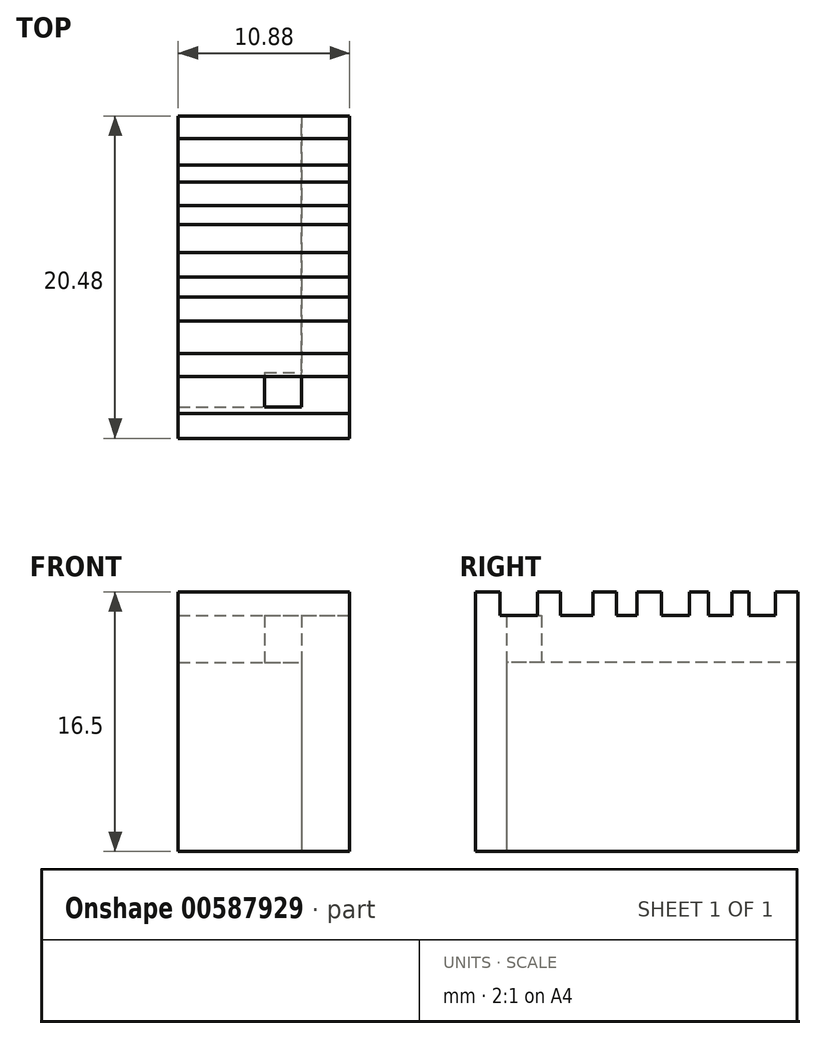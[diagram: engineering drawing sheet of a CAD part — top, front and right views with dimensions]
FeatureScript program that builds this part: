
annotation { "Feature Type Name" : "Feature", "Feature Type Description" : "" }
export const myFeature = defineFeature(function(context is Context, id is Id, definition is map)
    precondition{}
    {
        {
            var Q0;
            Q0=qCreatedBy(makeId("Top.planeOp"),FACE);
            var sketch = newSketch(context, id + "F0", { "sketchPlane" : qUnion([Q0])});
            skLineSegment(sketch, "E0.bottom", {"start": v(-21.97, 0.96) * mm, "end": v(-16.47, 0.96) * mm});
            skLineSegment(sketch, "E0.top", {"start": v(-21.97, -15.34) * mm, "end": v(-16.47, -15.34) * mm});
            skLineSegment(sketch, "E0.left", {"start": v(-21.97, 0.96) * mm, "end": v(-21.97, -15.34) * mm});
            skLineSegment(sketch, "E0.right", {"start": v(-16.47, 0.96) * mm, "end": v(-16.47, -15.34) * mm});
            skLineSegment(sketch, "E1.bottom", {"start": v(-16.47, 0.96) * mm, "end": v(-14.14, 0.96) * mm});
            skLineSegment(sketch, "E1.top", {"start": v(-16.47, -15.34) * mm, "end": v(-14.14, -15.34) * mm});
            skLineSegment(sketch, "E1.right", {"start": v(-14.14, 0.96) * mm, "end": v(-14.14, -15.34) * mm});
            skLineSegment(sketch, "E2.top", {"start": v(-21.97, -17.55) * mm, "end": v(-16.47, -17.55) * mm});
            skLineSegment(sketch, "E2.left", {"start": v(-21.97, -15.34) * mm, "end": v(-21.97, -17.55) * mm});
            skLineSegment(sketch, "E2.right", {"start": v(-16.47, -15.34) * mm, "end": v(-16.47, -17.55) * mm});
            skLineSegment(sketch, "E3.bottom", {"start": v(-21.97, -17.55) * mm, "end": v(-11.09, -17.55) * mm});
            skLineSegment(sketch, "E3.top", {"start": v(-21.97, -19.52) * mm, "end": v(-11.09, -19.52) * mm});
            skLineSegment(sketch, "E3.left", {"start": v(-21.97, -17.55) * mm, "end": v(-21.97, -19.52) * mm});
            skLineSegment(sketch, "E3.right", {"start": v(-11.09, -17.55) * mm, "end": v(-11.09, -19.52) * mm});
            skLineSegment(sketch, "E4.bottom", {"start": v(-11.09, -17.55) * mm, "end": v(-14.14, -17.55) * mm});
            skLineSegment(sketch, "E4.top", {"start": v(-11.09, 0.96) * mm, "end": v(-14.14, 0.96) * mm});
            skLineSegment(sketch, "E4.left", {"start": v(-11.09, -17.55) * mm, "end": v(-11.09, 0.96) * mm});
            skLineSegment(sketch, "E4.right", {"start": v(-14.14, -17.55) * mm, "end": v(-14.14, 0.96) * mm});
            skPoint(sketch, "E5", {"position": v(-14.14, -17.55) * mm});
            skLineSegment(sketch, "E6.bottom", {"start": v(-16.47, -17.55) * mm, "end": v(-14.14, -17.55) * mm});
            skLineSegment(sketch, "E6.left", {"start": v(-16.47, -17.55) * mm, "end": v(-16.47, -15.34) * mm});
            skLineSegment(sketch, "E6.right", {"start": v(-14.14, -17.55) * mm, "end": v(-14.14, -15.34) * mm});
            skSolve(sketch);
        }
        {
            var Q0;
            Q0 = qSketchRegion(id + "F0", true);
            var Q1;
            Q1=makeQuery(id+"F0.imprint","IMPRINT",FACE,{"disambiguationData":[TD([[makeQuery(id+"F0.imprint","IMPRINT",EDGE,{"derivedFrom":sQuery(id+"F0.wireOp",EDGE,"E6.bottom")}),1.0]])]});
            extrude(context, id + "F1", {"entities" : qUnion([Q0, Q1]), "depth" : 15 * mm, "offsetDistance" : 25 * mm});
        }
        {
            var Q0;
            {var subQ4=sQuery(id+"F0.wireOp",EDGE,"E1.bottom");Q0=makeQuery(id+"F0.imprint","IMPRINT",FACE,{"disambiguationData":[TD([[makeQuery(id+"F0.imprint","IMPRINT",EDGE,{"derivedFrom":subQ4}),-1.0]])]});}
            var Q1;
            Q1=makeQuery(id+"F0.imprint","IMPRINT",FACE,{"disambiguationData":[TD([[makeQuery(id+"F0.imprint","IMPRINT",EDGE,{"derivedFrom":sQuery(id+"F0.wireOp",EDGE,"E0.bottom")}),-1.0]])]});
            var Q2;
            {var subQ4=sQuery(id+"F0.wireOp",EDGE,"E0.top");Q2=makeQuery(id+"F0.imprint","IMPRINT",FACE,{"disambiguationData":[TD([[makeQuery(id+"F0.imprint","IMPRINT",EDGE,{"derivedFrom":subQ4}),-1.0]])]});}
            var Q3;
            {var subQ0=sQuery(id+"F0.wireOp",EDGE,"E1.top");Q3=makeQuery(id+"F0.imprint","IMPRINT",FACE,{"disambiguationData":[TD([[makeQuery(id+"F0.imprint","IMPRINT",EDGE,{"derivedFrom":subQ0}),-1.0]])]});}
            var Q4;
            Q4=makeQuery(id+"F0.imprint","IMPRINT",FACE,{"disambiguationData":[TD([[makeQuery(id+"F0.imprint","IMPRINT",EDGE,{"derivedFrom":sQuery(id+"F0.wireOp",EDGE,"E6.bottom")}),1.0]])]});
            extrude(context, id + "F2", {"entities" : qUnion([Q0, Q1, Q2, Q3, Q4]), "operationType" : NewBodyOperationType.REMOVE, "depth" : 12 * mm, "offsetDistance" : 25 * mm});
        }
        {
            var Q0;
            Q0=makeQuery(id+"F1.opExtrude","CAP_FACE",FACE,{"disambiguationData":[OSD([sQuery(id+"F0.wireOp",EDGE,"E0.bottom"),sQuery(id+"F0.wireOp",EDGE,"E0.left"),sQuery(id+"F0.wireOp",EDGE,"E1.bottom"),sQuery(id+"F0.wireOp",EDGE,"E2.left"),sQuery(id+"F0.wireOp",EDGE,"E3.top"),sQuery(id+"F0.wireOp",EDGE,"E3.left"),sQuery(id+"F0.wireOp",EDGE,"E3.right"),sQuery(id+"F0.wireOp",EDGE,"E4.top"),sQuery(id+"F0.wireOp",EDGE,"E4.left")])],"isStart":false});
            var sketch = newSketch(context, id + "F3", { "sketchPlane" : qUnion([Q0])});
            skLineSegment(sketch, "E7.bottom", {"start": v(-21.97, -19.52) * mm, "end": v(-11.09, -19.52) * mm});
            skLineSegment(sketch, "E7.top", {"start": v(-21.97, -17.95) * mm, "end": v(-11.09, -17.95) * mm});
            skLineSegment(sketch, "E7.left", {"start": v(-21.97, -19.52) * mm, "end": v(-21.97, -17.95) * mm});
            skLineSegment(sketch, "E7.right", {"start": v(-11.09, -19.52) * mm, "end": v(-11.09, -17.95) * mm});
            skLineSegment(sketch, "E8.bottom", {"start": v(-21.97, -15.6) * mm, "end": v(-11.09, -15.6) * mm});
            skLineSegment(sketch, "E8.top", {"start": v(-21.97, -14.13) * mm, "end": v(-11.09, -14.13) * mm});
            skLineSegment(sketch, "E8.left", {"start": v(-21.97, -15.6) * mm, "end": v(-21.97, -14.13) * mm});
            skLineSegment(sketch, "E8.right", {"start": v(-11.09, -15.6) * mm, "end": v(-11.09, -14.13) * mm});
            skLineSegment(sketch, "E9.bottom", {"start": v(-21.97, -12.08) * mm, "end": v(-11.09, -12.08) * mm});
            skLineSegment(sketch, "E9.top", {"start": v(-21.97, -10.56) * mm, "end": v(-11.09, -10.56) * mm});
            skLineSegment(sketch, "E9.left", {"start": v(-21.97, -12.08) * mm, "end": v(-21.97, -10.56) * mm});
            skLineSegment(sketch, "E9.right", {"start": v(-11.09, -12.08) * mm, "end": v(-11.09, -10.56) * mm});
            skLineSegment(sketch, "E10.bottom", {"start": v(-21.97, -9.28) * mm, "end": v(-11.09, -9.28) * mm});
            skLineSegment(sketch, "E10.top", {"start": v(-21.97, -7.72) * mm, "end": v(-11.09, -7.72) * mm});
            skLineSegment(sketch, "E10.left", {"start": v(-21.97, -9.28) * mm, "end": v(-21.97, -7.72) * mm});
            skLineSegment(sketch, "E10.right", {"start": v(-11.09, -9.28) * mm, "end": v(-11.09, -7.72) * mm});
            skLineSegment(sketch, "E11.bottom", {"start": v(-21.97, -5.94) * mm, "end": v(-11.09, -5.94) * mm});
            skLineSegment(sketch, "E11.top", {"start": v(-21.97, -4.74) * mm, "end": v(-11.09, -4.74) * mm});
            skLineSegment(sketch, "E11.left", {"start": v(-21.97, -5.94) * mm, "end": v(-21.97, -4.74) * mm});
            skLineSegment(sketch, "E11.right", {"start": v(-11.09, -5.94) * mm, "end": v(-11.09, -4.74) * mm});
            skLineSegment(sketch, "E12.bottom", {"start": v(-21.97, -2.15) * mm, "end": v(-11.09, -2.15) * mm});
            skLineSegment(sketch, "E12.top", {"start": v(-21.97, -3.24) * mm, "end": v(-11.09, -3.24) * mm});
            skLineSegment(sketch, "E12.left", {"start": v(-21.97, -2.15) * mm, "end": v(-21.97, -3.24) * mm});
            skLineSegment(sketch, "E12.right", {"start": v(-11.09, -2.15) * mm, "end": v(-11.09, -3.24) * mm});
            skLineSegment(sketch, "E13.bottom", {"start": v(-21.97, 0.96) * mm, "end": v(-11.09, 0.96) * mm});
            skLineSegment(sketch, "E13.top", {"start": v(-21.97, -0.48) * mm, "end": v(-11.09, -0.48) * mm});
            skLineSegment(sketch, "E13.left", {"start": v(-21.97, 0.96) * mm, "end": v(-21.97, -0.48) * mm});
            skLineSegment(sketch, "E13.right", {"start": v(-11.09, 0.96) * mm, "end": v(-11.09, -0.48) * mm});
            skSolve(sketch);
        }
        {
            var Q0;
            Q0 = qSketchRegion(id + "F3", true);
            extrude(context, id + "F4", {"entities" : qUnion([Q0]), "operationType" : NewBodyOperationType.ADD, "depth" : 1.5 * mm, "offsetDistance" : 25 * mm});
        }
    });
